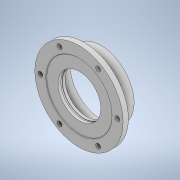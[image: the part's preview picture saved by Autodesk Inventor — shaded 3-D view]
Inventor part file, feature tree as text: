
AUTODESK INVENTOR PART (.ipt)
format: ipt  version: 2020 (Build 240168000, 168)  size: 201,216 bytes
history: native  units: mm
features: extrude x7, sketch x7, other x3, plane x2, reference x2, fillet x1, projected_geometry x1
ambient origin geometry x8: Origin, YZ Plane, XZ Plane, XY Plane, X Axis, Y Axis, Z Axis, Center Point
bodies: 实体1 (feature_tree)
feature tree (23):
  plane  "工作平面1"
  extrude  "拉伸1"  Depth=11.0mm
  extrude  "拉伸2"  Depth=12.0mm TaperAngle=0.0deg
  extrude  "拉伸3"  Depth=12.0mm
  extrude  "拉伸4"  Depth=38.0mm TaperAngle=0.0deg
  fillet  "圆角1"  Radius=150.0mm
  extrude  "拉伸5"  Depth=1.0mm
  plane  "工作平面2"
  extrude  "拉伸6"  Depth=5.0mm TaperAngle=0.0deg
  extrude  "拉伸7"  Depth=3.55mm TaperAngle=0.0deg
  sketch  "草图1"  dims[d0=175.0mm d1=11.0mm]
  reference  "参考1"
  sketch  "草图2"  dims[d2=60.0mm d4=360.0deg d6=12.0mm d7=0.0mm]
  reference  "参考2"
  sketch  "草图3"  dims[d9=12.0mm d10=0.0mm d11=150.0mm]
  sketch  "草图4"  dims[d12=140.0mm d13=38.0mm d14=0.0mm d15=150.0mm]
  sketch  "草图5"  dims[d16=1.0mm d17=0.0mm d18=1.0mm]
  projected_geometry  "投影回路1"
  sketch  "草图6"  dims[d19=97.0mm d20=5.0mm d21=0.0mm]
  sketch  "草图7"  dims[d22=98.55mm d23=3.55mm d24=0.0mm d25=1.0mm d26=2.0mm d27=0.0mm]
  other  "<userpath>\Desktop\ME_course_project\课设试试\shaft_try_1.iam"
  other  "shaft_try_1.iam"
  other  "xia(1):1"
